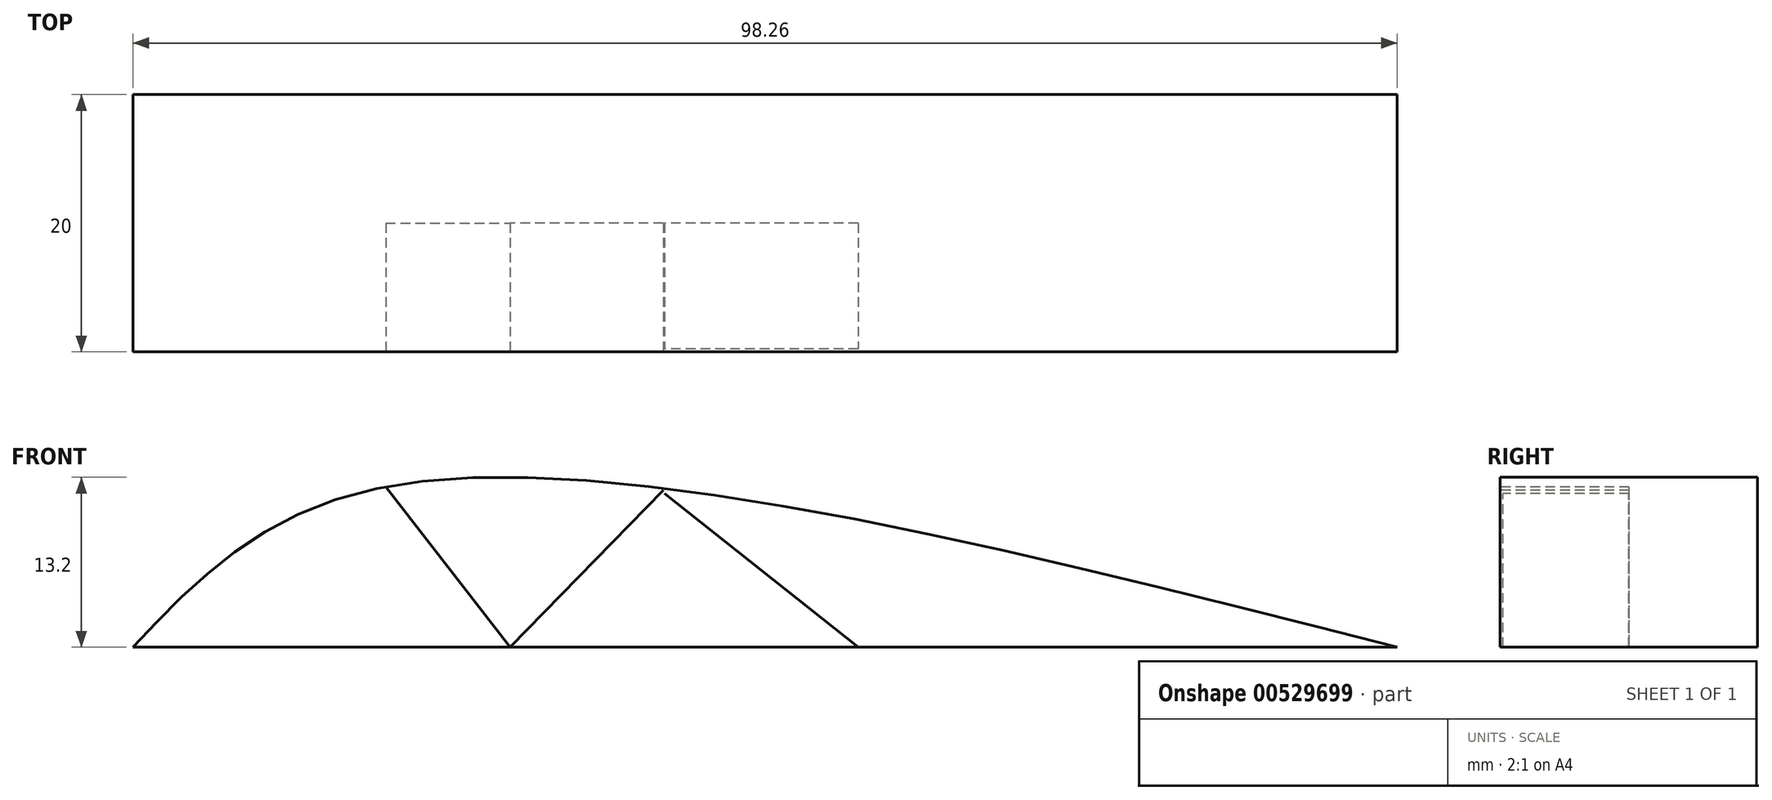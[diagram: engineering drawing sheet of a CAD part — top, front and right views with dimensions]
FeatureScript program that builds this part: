
annotation { "Feature Type Name" : "Feature", "Feature Type Description" : "" }
export const myFeature = defineFeature(function(context is Context, id is Id, definition is map)
    precondition{}
    {
        {
            var Q0;
            Q0=qCreatedBy(makeId("Front.planeOp"),FACE);
            var sketch = newSketch(context, id + "F0", { "sketchPlane" : qUnion([Q0])});
            skLineSegment(sketch, "E0", {"start": v(-46.84, 0) * mm, "end": v(51.42, 0) * mm});
            skFitSpline(sketch, "E1", {"points": [v(-46.84, 0) * mm, v(-28.1, 12.28) * mm, v(51.42, 0) * mm], "startDerivative": vector(42.63, 44.94) * mm, "endDerivative": vector(143.5, -36.54) * mm});
            skSolve(sketch);
        }
        {
            var Q0;
            Q0=sQuery(id+"F0.wireOp",EDGE,"E1");
            var Q1;
            Q1=sQuery(id+"F0.wireOp",EDGE,"E0");
            extrude(context, id + "F1", {"bodyType" : ToolBodyType.SURFACE, "surfaceEntities" : qUnion([Q0, Q1]), "endBound" : BoundingType.SYMMETRIC, "depth" : 20 * mm, "offsetDistance" : 25 * mm});
        }
        {
            var Q0;
            Q0=qCreatedBy(makeId("Front.planeOp"),FACE);
            var sketch = newSketch(context, id + "F2", { "sketchPlane" : qUnion([Q0])});
            skLineSegment(sketch, "E2", {"start": v(-27.18, 12.44) * mm, "end": v(-17.52, 0) * mm});
            skSolve(sketch);
        }
        {
            var Q0;
            Q0=sQuery(id+"F2.wireOp",EDGE,"E2");
            extrude(context, id + "F3", {"bodyType" : ToolBodyType.SURFACE, "surfaceEntities" : qUnion([Q0]), "depth" : 10 * mm, "offsetDistance" : 25 * mm});
        }
        {
            var Q0;
            Q0=qCreatedBy(makeId("Front.planeOp"),FACE);
            var sketch = newSketch(context, id + "F4", { "sketchPlane" : qUnion([Q0])});
            skLineSegment(sketch, "E3", {"start": v(-5.63, 12.17) * mm, "end": v(-17.53, 0) * mm});
            skSolve(sketch);
        }
        {
            var Q0;
            Q0=sQuery(id+"F4.wireOp",EDGE,"E3");
            extrude(context, id + "F5", {"bodyType" : ToolBodyType.SURFACE, "surfaceEntities" : qUnion([Q0]), "depth" : 9.98 * mm, "offsetDistance" : 25 * mm});
        }
        {
            var Q0;
            Q0=qCreatedBy(makeId("Front.planeOp"),FACE);
            var sketch = newSketch(context, id + "F6", { "sketchPlane" : qUnion([Q0])});
            skLineSegment(sketch, "E4", {"start": v(9.53, 0) * mm, "end": v(-5.53, 11.93) * mm});
            skSolve(sketch);
        }
        {
            var Q0;
            Q0=sQuery(id+"F6.wireOp",EDGE,"E4");
            extrude(context, id + "F7", {"bodyType" : ToolBodyType.SURFACE, "surfaceEntities" : qUnion([Q0]), "depth" : 9.78 * mm, "offsetDistance" : 25 * mm});
        }
    });
